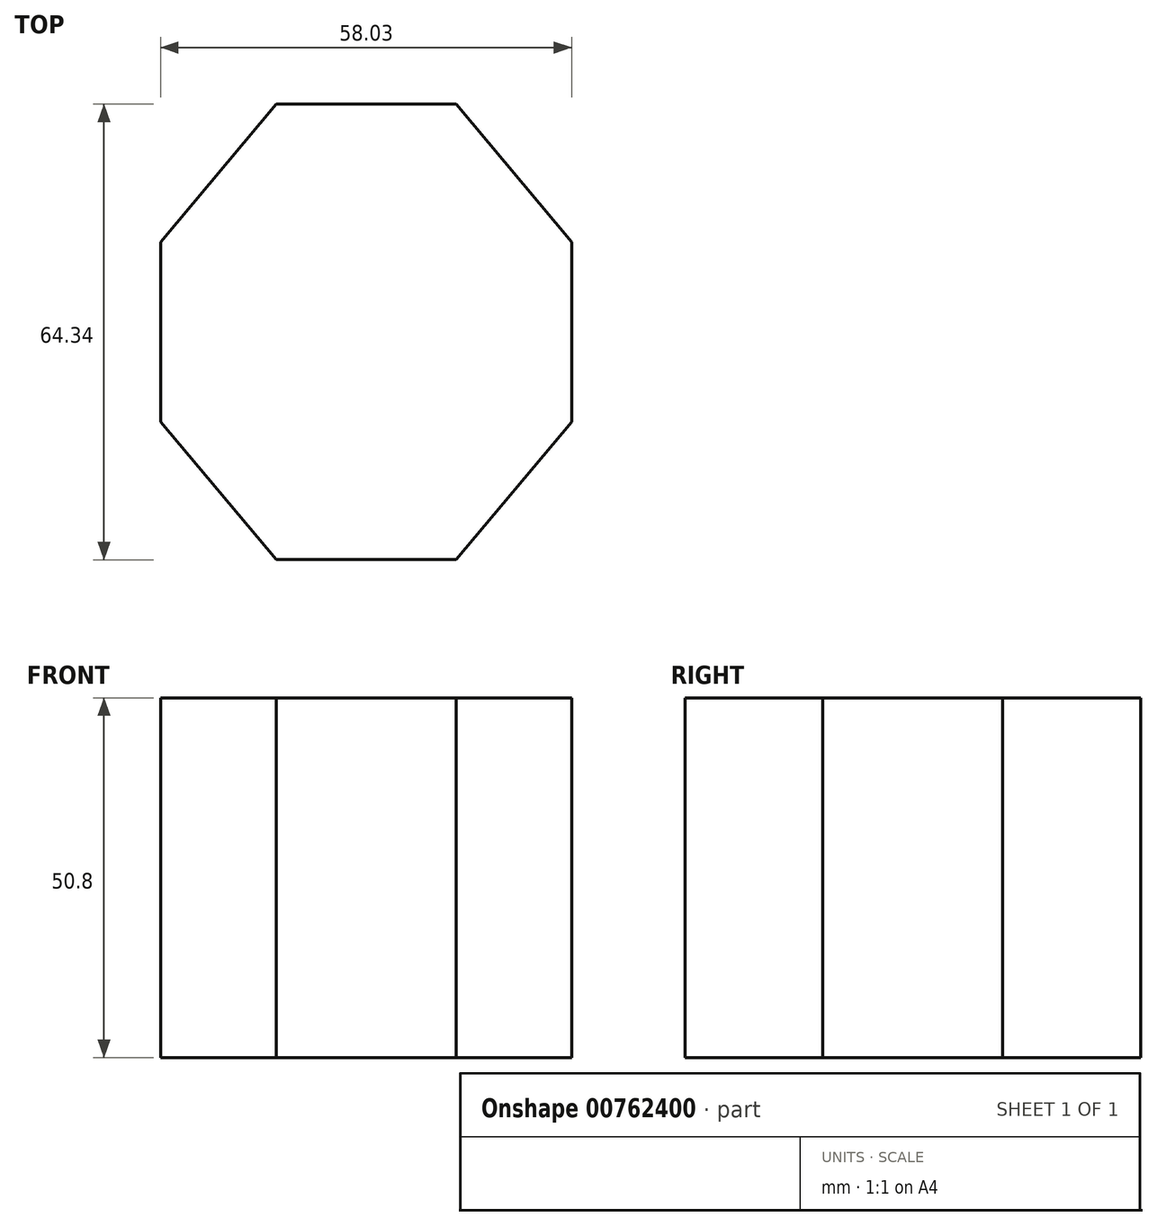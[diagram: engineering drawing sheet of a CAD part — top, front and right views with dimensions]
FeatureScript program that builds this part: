
annotation { "Feature Type Name" : "Feature", "Feature Type Description" : "" }
export const myFeature = defineFeature(function(context is Context, id is Id, definition is map)
    precondition{}
    {
        {
            var Q0;
            Q0=qCreatedBy(makeId("Top.planeOp"),FACE);
            var sketch = newSketch(context, id + "F0", { "sketchPlane" : qUnion([Q0])});
            skLineSegment(sketch, "E0", {"start": v(-42.73, 44.87) * mm, "end": v(-17.33, 44.87) * mm});
            skLineSegment(sketch, "E1", {"start": v(-17.33, 44.87) * mm, "end": v(-1.02, 25.4) * mm});
            skLineSegment(sketch, "E2", {"start": v(-1.02, 25.4) * mm, "end": v(-1.02, 0) * mm});
            skLineSegment(sketch, "E3", {"start": v(-1.02, 0) * mm, "end": v(-17.33, -19.47) * mm});
            skLineSegment(sketch, "E4", {"start": v(-17.33, -19.47) * mm, "end": v(-42.73, -19.47) * mm});
            skLineSegment(sketch, "E5", {"start": v(-42.73, -19.47) * mm, "end": v(-59.05, 0) * mm});
            skLineSegment(sketch, "E6", {"start": v(-59.05, 0) * mm, "end": v(-59.05, 25.4) * mm});
            skLineSegment(sketch, "E7", {"start": v(-59.05, 25.4) * mm, "end": v(-42.73, 44.87) * mm});
            skSolve(sketch);
        }
        {
            var Q0;
            Q0 = qSketchRegion(id + "F0", true);
            extrude(context, id + "F1", {"entities" : qUnion([Q0]), "depth" : 50.8 * mm, "offsetDistance" : 25.4 * mm});
        }
    });
